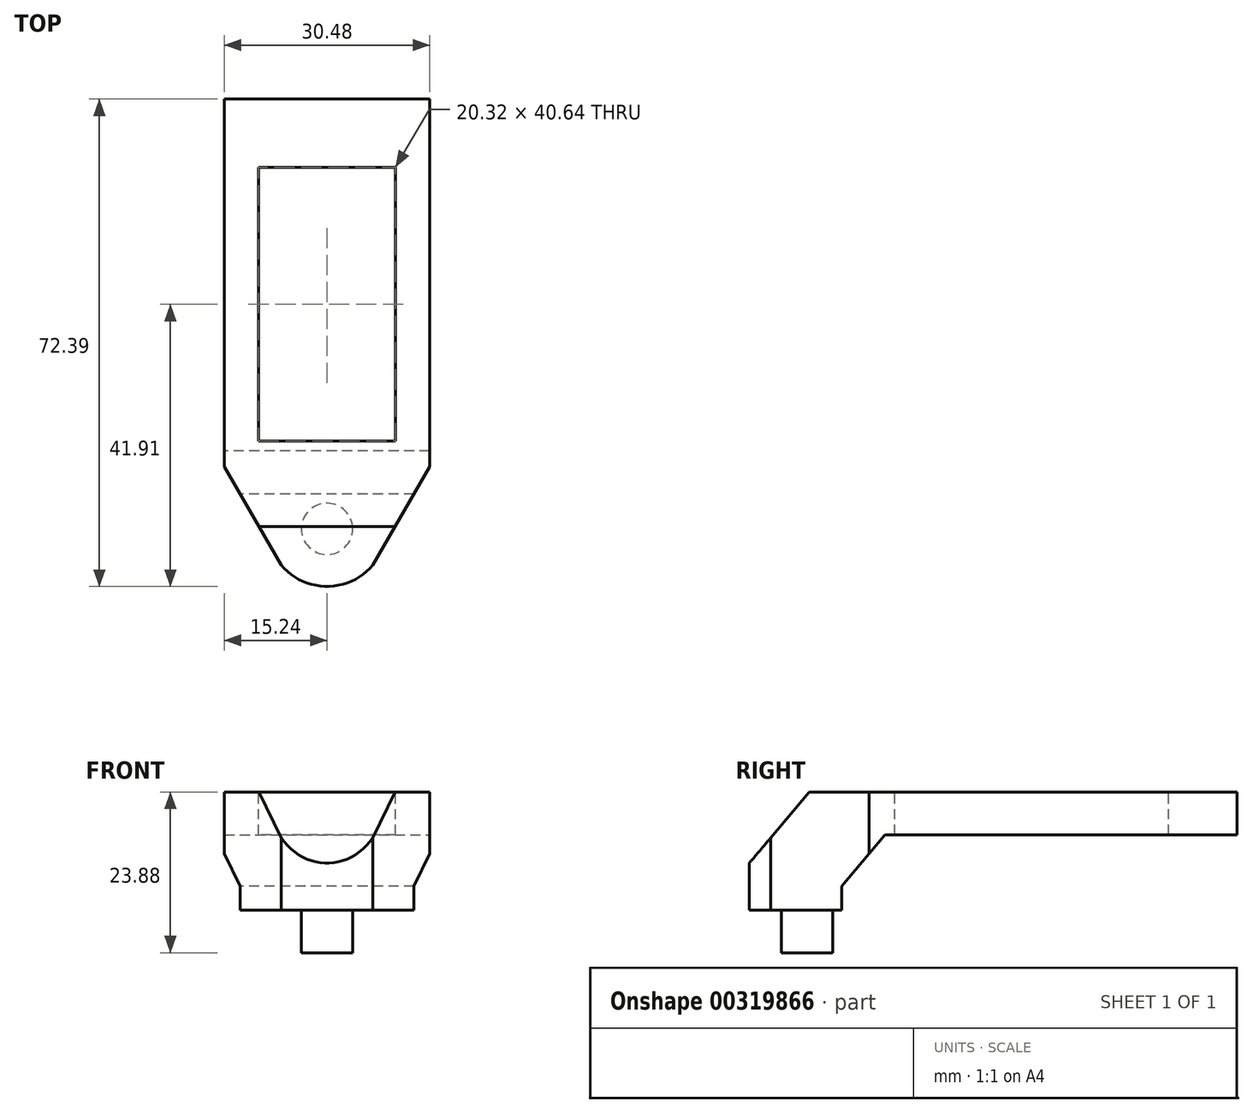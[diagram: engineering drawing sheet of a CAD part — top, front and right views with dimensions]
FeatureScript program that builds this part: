
annotation { "Feature Type Name" : "Feature", "Feature Type Description" : "" }
export const myFeature = defineFeature(function(context is Context, id is Id, definition is map)
    precondition{}
    {
        {
            var Q0;
            Q0=qCreatedBy(makeId("Top.planeOp"),FACE);
            var sketch = newSketch(context, id + "F0", { "sketchPlane" : qUnion([Q0])});
            skCircle(sketch, "E0", {"center": v(0, 0) * mm, "radius": 6.35 * mm, "construction": true});
            skLineSegment(sketch, "E1", {"start": v(0, 0) * mm, "end": v(0, -22.86) * mm, "construction": true});
            skCircle(sketch, "E2", {"center": v(0, -22.86) * mm, "radius": 3.81 * mm, "construction": true});
            skLineSegment(sketch, "E3.bottom", {"start": v(10.16, -10.16) * mm, "end": v(-10.16, -10.16) * mm});
            skLineSegment(sketch, "E3.top", {"start": v(10.16, 30.48) * mm, "end": v(-10.16, 30.48) * mm});
            skLineSegment(sketch, "E3.left", {"start": v(10.16, -10.16) * mm, "end": v(10.16, 30.48) * mm});
            skLineSegment(sketch, "E3.right", {"start": v(-10.16, -10.16) * mm, "end": v(-10.16, 30.48) * mm});
            skPoint(sketch, "E3.middle", {"position": v(0, 10.16) * mm});
            skLineSegment(sketch, "E4.bottom", {"start": v(-15.24, -13.97) * mm, "end": v(15.24, -13.97) * mm});
            skLineSegment(sketch, "E4.top", {"start": v(-15.24, 40.64) * mm, "end": v(15.24, 40.64) * mm});
            skLineSegment(sketch, "E4.left", {"start": v(-15.24, -13.97) * mm, "end": v(-15.24, 40.64) * mm});
            skLineSegment(sketch, "E4.right", {"start": v(15.24, -13.97) * mm, "end": v(15.24, 40.64) * mm});
            skPoint(sketch, "E4.middle", {"position": v(0, 13.33) * mm});
            skLineSegment(sketch, "E5", {"start": v(-15.24, -13.97) * mm, "end": v(-6.8, -28.58) * mm});
            skLineSegment(sketch, "E6", {"start": v(6.8, -28.58) * mm, "end": v(15.24, -13.97) * mm});
            skPoint(sketch, "E7.orphan", {"position": v(0, -40.37) * mm});
            skArc(sketch, "E8.trimOffspring", {"start": v(-6.8, -28.58) * mm, "mid": v(0, -31.75) * mm, "end": v(6.8, -28.58) * mm});
            skSolve(sketch);
        }
        {
            var Q0;
            Q0=qCreatedBy(makeId("Right.planeOp"),FACE);
            var sketch = newSketch(context, id + "F1", { "sketchPlane" : qUnion([Q0])});
            skLineSegment(sketch, "E9.bottom", {"start": v(40.78, 0) * mm, "end": v(-26.5, 0) * mm});
            skLineSegment(sketch, "E9.top", {"start": v(40.78, -13.66) * mm, "end": v(-26.5, -13.66) * mm});
            skLineSegment(sketch, "E9.left", {"start": v(40.78, 0) * mm, "end": v(40.78, -13.66) * mm});
            skLineSegment(sketch, "E9.right", {"start": v(-26.5, 0) * mm, "end": v(-26.5, -13.66) * mm});
            skSolve(sketch);
        }
        {
            var Q0;
            Q0 = qSketchRegion(id + "F0", true);
            extrude(context, id + "F2", {"entities" : qUnion([Q0]), "oppositeDirection" : true, "depth" : 17.53 * mm});
        }
        {
            var Q0;
            Q0=qCreatedBy(makeId("Right.planeOp"),FACE);
            var sketch = newSketch(context, id + "F3", { "sketchPlane" : qUnion([Q0])});
            skLineSegment(sketch, "E10", {"start": v(0, 0) * mm, "end": v(-22.86, 0) * mm});
            skLineSegment(sketch, "E11", {"start": v(0, 0) * mm, "end": v(40.78, 0) * mm});
            skLineSegment(sketch, "E12", {"start": v(40.78, 0) * mm, "end": v(40.78, -6.35) * mm});
            skLineSegment(sketch, "E13", {"start": v(-22.86, 0) * mm, "end": v(-31.91, -10.79) * mm});
            skLineSegment(sketch, "E14", {"start": v(40.78, -6.35) * mm, "end": v(-11.6, -6.35) * mm});
            skLineSegment(sketch, "E15", {"start": v(-11.6, -6.35) * mm, "end": v(-18, -13.97) * mm});
            skLineSegment(sketch, "E16", {"start": v(-31.7, -13.97) * mm, "end": v(-12.35, -13.97) * mm, "construction": true});
            skLineSegment(sketch, "E17", {"start": v(-18, -13.97) * mm, "end": v(-18, -17.53) * mm});
            skLineSegment(sketch, "E18", {"start": v(-18, -17.53) * mm, "end": v(-31.91, -17.53) * mm});
            skLineSegment(sketch, "E19", {"start": v(-31.91, -10.79) * mm, "end": v(-31.91, -17.53) * mm});
            skSolve(sketch);
        }
        {
            var Q0;
            Q0 = qSketchRegion(id + "F3", true);
            extrude(context, id + "F4", {"entities" : qUnion([Q0]), "operationType" : NewBodyOperationType.INTERSECT, "endBound" : BoundingType.THROUGH_ALL, "depth" : 25.4 * mm, "hasSecondDirection" : true, "secondDirectionOppositeDirection" : true, "secondDirectionDepth" : 25.4 * mm});
        }
        {
            var Q0;
            Q0=makeQuery(id+"F2.opExtrude","CAP_FACE",FACE,{"disambiguationData":[OSD([sQuery(id+"F0.wireOp",EDGE,"E3.bottom"),sQuery(id+"F0.wireOp",EDGE,"E3.top"),sQuery(id+"F0.wireOp",EDGE,"E3.left"),sQuery(id+"F0.wireOp",EDGE,"E3.right"),sQuery(id+"F0.wireOp",EDGE,"E4.top"),sQuery(id+"F0.wireOp",EDGE,"E4.left"),sQuery(id+"F0.wireOp",EDGE,"E4.right"),sQuery(id+"F0.wireOp",EDGE,"E5"),sQuery(id+"F0.wireOp",EDGE,"E6"),sQuery(id+"F0.wireOp",EDGE,"E8.trimOffspring")])],"isStart":false});
            var sketch = newSketch(context, id + "F5", { "sketchPlane" : qUnion([Q0])});
            skCircle(sketch, "E20", {"center": v(0, 23.18) * mm, "radius": 3.81 * mm});
            skSolve(sketch);
        }
        {
            var Q0;
            Q0 = qSketchRegion(id + "F5", true);
            extrude(context, id + "F6", {"entities" : qUnion([Q0]), "operationType" : NewBodyOperationType.ADD, "depth" : 6.35 * mm});
        }
    });
